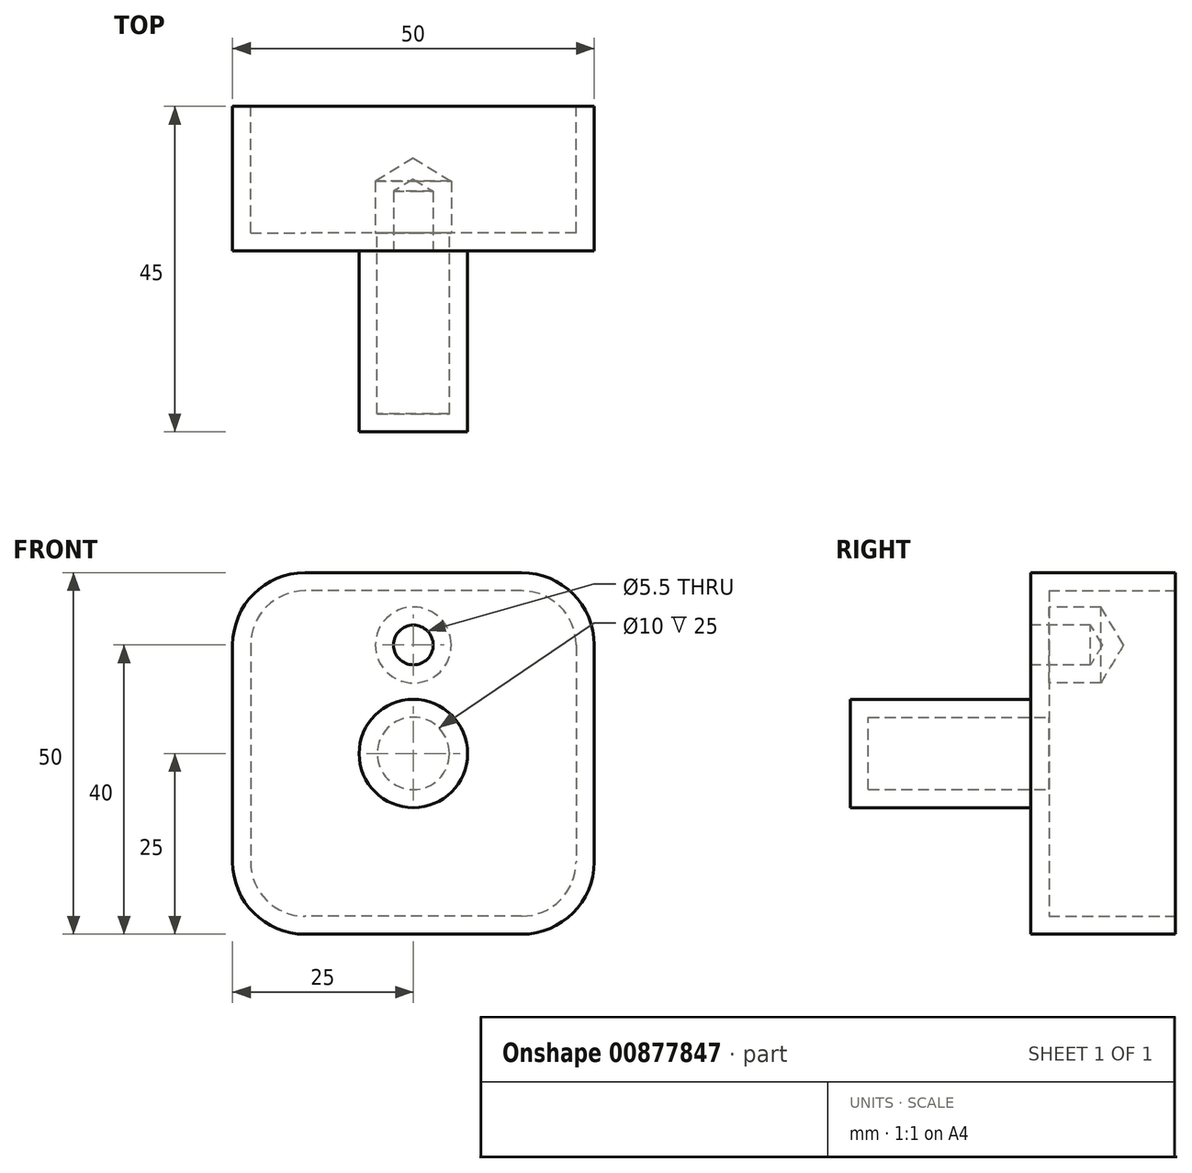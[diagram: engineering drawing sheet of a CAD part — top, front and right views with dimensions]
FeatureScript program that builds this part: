
annotation { "Feature Type Name" : "Feature", "Feature Type Description" : "" }
export const myFeature = defineFeature(function(context is Context, id is Id, definition is map)
    precondition{}
    {
        {
            var Q0;
            Q0=qCreatedBy(makeId("Front.planeOp"),FACE);
            var sketch = newSketch(context, id + "F0", { "sketchPlane" : qUnion([Q0])});
            skLineSegment(sketch, "E0.bottom", {"start": v(25, 25) * mm, "end": v(-25, 25) * mm});
            skLineSegment(sketch, "E0.top", {"start": v(25, -25) * mm, "end": v(-25, -25) * mm});
            skLineSegment(sketch, "E0.left", {"start": v(25, 25) * mm, "end": v(25, -25) * mm});
            skLineSegment(sketch, "E0.right", {"start": v(-25, 25) * mm, "end": v(-25, -25) * mm});
            skPoint(sketch, "E0.middle", {"position": v(0, 0) * mm});
            skSolve(sketch);
        }
        {
            var Q0;
            Q0 = qSketchRegion(id + "F0", true);
            extrude(context, id + "F1", {"entities" : qUnion([Q0]), "oppositeDirection" : true, "depth" : 20 * mm, "offsetDistance" : 25 * mm});
        }
        {
            var Q0;
            Q0=makeQuery(id+"F1.opExtrude","CAP_FACE",FACE,{"disambiguationData":[OSD([sQuery(id+"F0.wireOp",EDGE,"E0.bottom"),sQuery(id+"F0.wireOp",EDGE,"E0.top"),sQuery(id+"F0.wireOp",EDGE,"E0.left"),sQuery(id+"F0.wireOp",EDGE,"E0.right")])],"isStart":true});
            var sketch = newSketch(context, id + "F2", { "sketchPlane" : qUnion([Q0])});
            skCircle(sketch, "E1", {"center": v(0, 0) * mm, "radius": 7.5 * mm});
            skSolve(sketch);
        }
        {
            var Q0;
            Q0 = qSketchRegion(id + "F2", true);
            extrude(context, id + "F3", {"entities" : qUnion([Q0]), "operationType" : NewBodyOperationType.ADD, "depth" : 25 * mm, "offsetDistance" : 25 * mm});
        }
        {
            var Q0;
            Q0=makeQuery(id+"F1.opExtrude","CAP_FACE",FACE,{"disambiguationData":[OSD([sQuery(id+"F0.wireOp",EDGE,"E0.bottom"),sQuery(id+"F0.wireOp",EDGE,"E0.top"),sQuery(id+"F0.wireOp",EDGE,"E0.left"),sQuery(id+"F0.wireOp",EDGE,"E0.right")])],"isStart":true});
            var sketch = newSketch(context, id + "F4", { "sketchPlane" : qUnion([Q0])});
            skLineSegment(sketch, "E2", {"start": v(0, 0) * mm, "end": v(0, 15) * mm});
            skSolve(sketch);
        }
        {
            var Q0;
            Q0=sQuery(id+"F4.wireOp",VERTEX,"E2.end");
            var Q1;
            Q1=makeQuery(id+"F1.opExtrude","SWEPT_BODY",BODY,{"disambiguationData":[OSD([sQuery(id+"F0.wireOp",EDGE,"E0.bottom"),sQuery(id+"F0.wireOp",EDGE,"E0.top"),sQuery(id+"F0.wireOp",EDGE,"E0.left"),sQuery(id+"F0.wireOp",EDGE,"E0.right")])]});
            hole(context, id + "F5", {"style" : HoleStyle.SIMPLE, "endStyle" : HoleEndStyle.BLIND, "standardTappedOrClearance" : lookupTablePath({ "standard" : "ISO", "engagement" : "50%", "pitch" : "0.75 mm", "size" : "M6", "type" : "Tapped" }), "standardBlindInLast" : lookupTablePath({ "standard" : "ISO", "engagement" : "50%", "pitch" : "0.75 mm", "size" : "M6", "type" : "Tapped" }), "holeDiameter" : 5.5 * mm, "majorDiameter" : 6 * mm, "showTappedDepth" : true, "holeDepth" : 8.25 * mm, "tappedDepth" : 6 * mm, "tapClearance" : 3, "locations" : qUnion([Q0]), "scope" : qUnion([Q1])});
        }
        {
            var Q0;
            Q0=makeQuery(id+"F1.opExtrude","SWEPT_EDGE",EDGE,{"disambiguationData":[OSD([sQuery(id+"F0.wireOp",EDGE,"E0.bottom"),sQuery(id+"F0.wireOp",EDGE,"E0.right")])]});
            var Q1;
            Q1=makeQuery(id+"F1.opExtrude","SWEPT_EDGE",EDGE,{"disambiguationData":[OSD([sQuery(id+"F0.wireOp",EDGE,"E0.bottom"),sQuery(id+"F0.wireOp",EDGE,"E0.left")])]});
            var Q2;
            Q2=makeQuery(id+"F1.opExtrude","SWEPT_EDGE",EDGE,{"disambiguationData":[OSD([sQuery(id+"F0.wireOp",EDGE,"E0.top"),sQuery(id+"F0.wireOp",EDGE,"E0.right")])]});
            var Q3;
            Q3=makeQuery(id+"F1.opExtrude","SWEPT_EDGE",EDGE,{"disambiguationData":[OSD([sQuery(id+"F0.wireOp",EDGE,"E0.top"),sQuery(id+"F0.wireOp",EDGE,"E0.left")])]});
            fillet(context, id + "F6", {"entities" : qUnion([Q0, Q1, Q2, Q3]), "radius" : 10 * mm, "tangentPropagation" : true, "allowEdgeOverflow" : false});
        }
        {
            var Q0;
            Q0=makeQuery(id+"F1.opExtrude","CAP_FACE",FACE,{"disambiguationData":[OSD([sQuery(id+"F0.wireOp",EDGE,"E0.bottom"),sQuery(id+"F0.wireOp",EDGE,"E0.top"),sQuery(id+"F0.wireOp",EDGE,"E0.left"),sQuery(id+"F0.wireOp",EDGE,"E0.right")])],"isStart":false});
            shell(context, id + "F7", {"entities" : qUnion([Q0]), "thickness" : 2.5 * mm});
        }
    });
